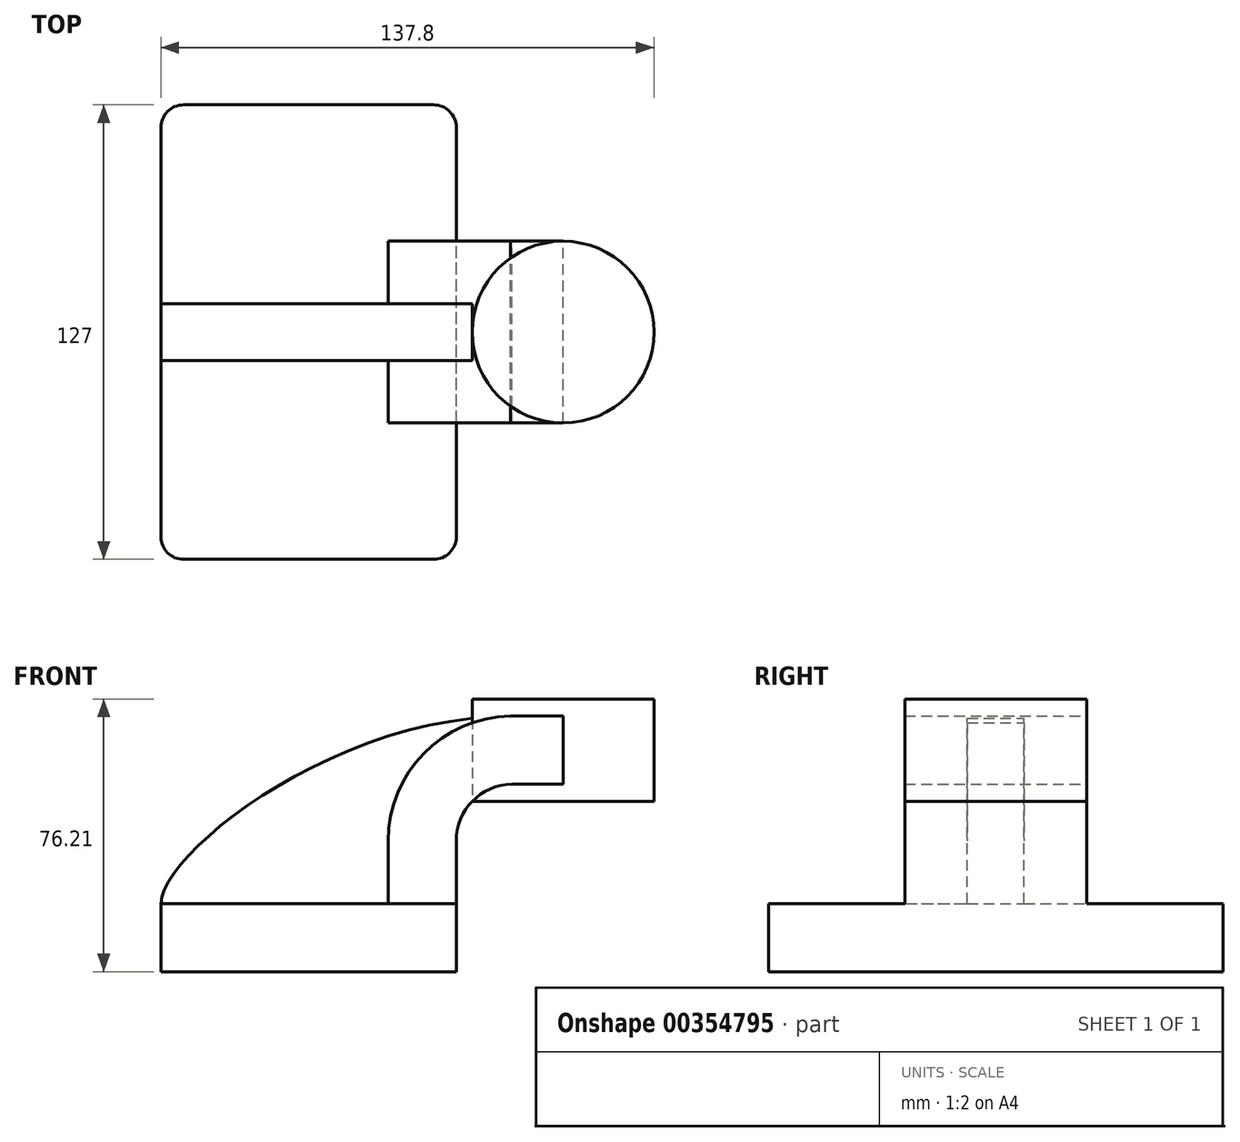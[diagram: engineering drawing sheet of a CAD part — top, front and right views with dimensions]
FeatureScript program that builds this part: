
annotation { "Feature Type Name" : "Feature", "Feature Type Description" : "" }
export const myFeature = defineFeature(function(context is Context, id is Id, definition is map)
    precondition{}
    {
        {
            var Q0;
            Q0=qCreatedBy(makeId("Front.planeOp"),FACE);
            var sketch = newSketch(context, id + "F0", { "sketchPlane" : qUnion([Q0])});
            skPoint(sketch, "E0.middle", {"position": v(0, 0) * mm});
            skLineSegment(sketch, "E1.top", {"start": v(10.35, 80.52) * mm, "end": v(16.64, 80.52) * mm});
            skLineSegment(sketch, "E2.bottom", {"start": v(-41.28, 9.52) * mm, "end": v(41.27, 9.53) * mm});
            skLineSegment(sketch, "E2.top", {"start": v(-41.28, -9.53) * mm, "end": v(41.28, -9.53) * mm});
            skLineSegment(sketch, "E2.left", {"start": v(-41.28, 9.52) * mm, "end": v(-41.27, -9.53) * mm});
            skLineSegment(sketch, "E2.right", {"start": v(41.28, 9.53) * mm, "end": v(41.28, -9.52) * mm});
            skLineSegment(sketch, "E3.bottom", {"start": v(45.72, 38.1) * mm, "end": v(96.52, 38.1) * mm});
            skLineSegment(sketch, "E3.top", {"start": v(45.72, 66.67) * mm, "end": v(96.52, 66.67) * mm});
            skLineSegment(sketch, "E3.left", {"start": v(45.72, 38.1) * mm, "end": v(45.72, 66.67) * mm});
            skLineSegment(sketch, "E3.right", {"start": v(96.52, 38.1) * mm, "end": v(96.52, 66.67) * mm});
            skPoint(sketch, "E3.middle", {"position": v(71.12, 52.39) * mm});
            skLineSegment(sketch, "E4", {"start": v(41.27, 9.53) * mm, "end": v(41.27, 27) * mm});
            skArc(sketch, "E5", {"start": v(41.27, 27) * mm, "mid": v(45.78, 38.09) * mm, "end": v(56.75, 42.88) * mm});
            skLineSegment(sketch, "E6", {"start": v(56.75, 42.88) * mm, "end": v(85.5, 42.88) * mm});
            skLineSegment(sketch, "E7.0", {"start": v(57.74, 61.93) * mm, "end": v(85.5, 61.93) * mm});
            skArc(sketch, "E7.1", {"start": v(22.23, 27) * mm, "mid": v(32.67, 51.91) * mm, "end": v(57.74, 61.93) * mm});
            skLineSegment(sketch, "E7.2", {"start": v(22.23, 9.53) * mm, "end": v(22.23, 27) * mm});
            skFitSpline(sketch, "E8", {"points": [v(-41.28, 9.53) * mm, v(57.74, 61.93) * mm], "startDerivative": vector(0.9, 41.85) * mm, "endDerivative": vector(153.01, -0.64) * mm});
            skLineSegment(sketch, "E9", {"start": v(71.12, 38.1) * mm, "end": v(71.12, 66.67) * mm});
            skPoint(sketch, "E9.endSnap0", {"position": v(71.12, 42.88) * mm});
            skSolve(sketch);
        }
        {
            var Q0;
            Q0=makeQuery(id+"F0.imprint","IMPRINT",FACE,{"disambiguationData":[TD([[makeQuery(id+"F0.imprint","IMPRINT",EDGE,{"derivedFrom":sQuery(id+"F0.wireOp",EDGE,"E2.top")}),1.0]])]});
            extrude(context, id + "F1", {"entities" : qUnion([Q0]), "endBound" : BoundingType.SYMMETRIC, "depth" : 127 * mm});
        }
        {
            var Q0;
            {var subQ0=sQuery(id+"F0.wireOp",EDGE,"E4");Q0=makeQuery(id+"F0.imprint","IMPRINT",FACE,{"disambiguationData":[TD([[makeQuery(id+"F0.imprint","IMPRINT",EDGE,{"derivedFrom":subQ0}),1.0]])]});}
            var Q1;
            {var subQ5=sQuery(id+"F0.wireOp",EDGE,"E3.bottom");var subQ7=sQuery(id+"F0.wireOp",EDGE,"E3.left");var subQ8=makeQuery(id+"F0.imprint","INTERSECT",VERTEX,{"derivedFrom":[subQ5,subQ7]});Q1=makeQuery(id+"F0.imprint","IMPRINT",FACE,{"disambiguationData":[TD([[makeQuery(id+"F0.imprint","IMPRINT",EDGE,{"disambiguationData":[TD([[subQ8,-1.0]])],"derivedFrom":subQ5}),1.0]])]});}
            extrude(context, id + "F2", {"entities" : qUnion([Q0, Q1]), "operationType" : NewBodyOperationType.ADD, "endBound" : BoundingType.SYMMETRIC, "depth" : 50.8 * mm});
        }
        {
            var Q0;
            {var subQ0=sQuery(id+"F0.wireOp",EDGE,"E7.2");Q0=makeQuery(id+"F0.imprint","IMPRINT",FACE,{"disambiguationData":[TD([[makeQuery(id+"F0.imprint","IMPRINT",EDGE,{"derivedFrom":subQ0}),1.0]])]});}
            extrude(context, id + "F3", {"entities" : qUnion([Q0]), "operationType" : NewBodyOperationType.ADD, "endBound" : BoundingType.SYMMETRIC, "depth" : 15.88 * mm});
        }
        {
            var Q0;
            {var subQ4=sQuery(id+"F0.wireOp",EDGE,"E3.right");Q0=makeQuery(id+"F0.imprint","IMPRINT",FACE,{"disambiguationData":[TD([[makeQuery(id+"F0.imprint","IMPRINT",EDGE,{"derivedFrom":subQ4}),1.0]])]});}
            var Q1;
            Q1=sQuery(id+"F0.wireOp",EDGE,"E9");
            revolve(context, id + "F4", {"entities" : qUnion([Q0]), "axis" : qUnion([Q1]), "revolveType" : RevolveType.FULL});
        }
        {
            var Q0;
            Q0=makeQuery(id+"F1.opExtrude","CAP_EDGE",EDGE,{"disambiguationData":[OSD([sQuery(id+"F0.wireOp",EDGE,"E2.left")])],"isStart":false});
            var Q1;
            Q1=makeQuery(id+"F1.opExtrude","CAP_EDGE",EDGE,{"disambiguationData":[OSD([sQuery(id+"F0.wireOp",EDGE,"E2.right")])],"isStart":false});
            var Q2;
            Q2=makeQuery(id+"F1.opExtrude","CAP_EDGE",EDGE,{"disambiguationData":[OSD([sQuery(id+"F0.wireOp",EDGE,"E2.right")])],"isStart":true});
            var Q3;
            Q3=makeQuery(id+"F1.opExtrude","CAP_EDGE",EDGE,{"disambiguationData":[OSD([sQuery(id+"F0.wireOp",EDGE,"E2.left")])],"isStart":true});
            fillet(context, id + "F5", {"entities" : qUnion([Q0, Q1, Q2, Q3]), "radius" : 6.35 * mm, "tangentPropagation" : true, "allowEdgeOverflow" : false});
        }
    });
